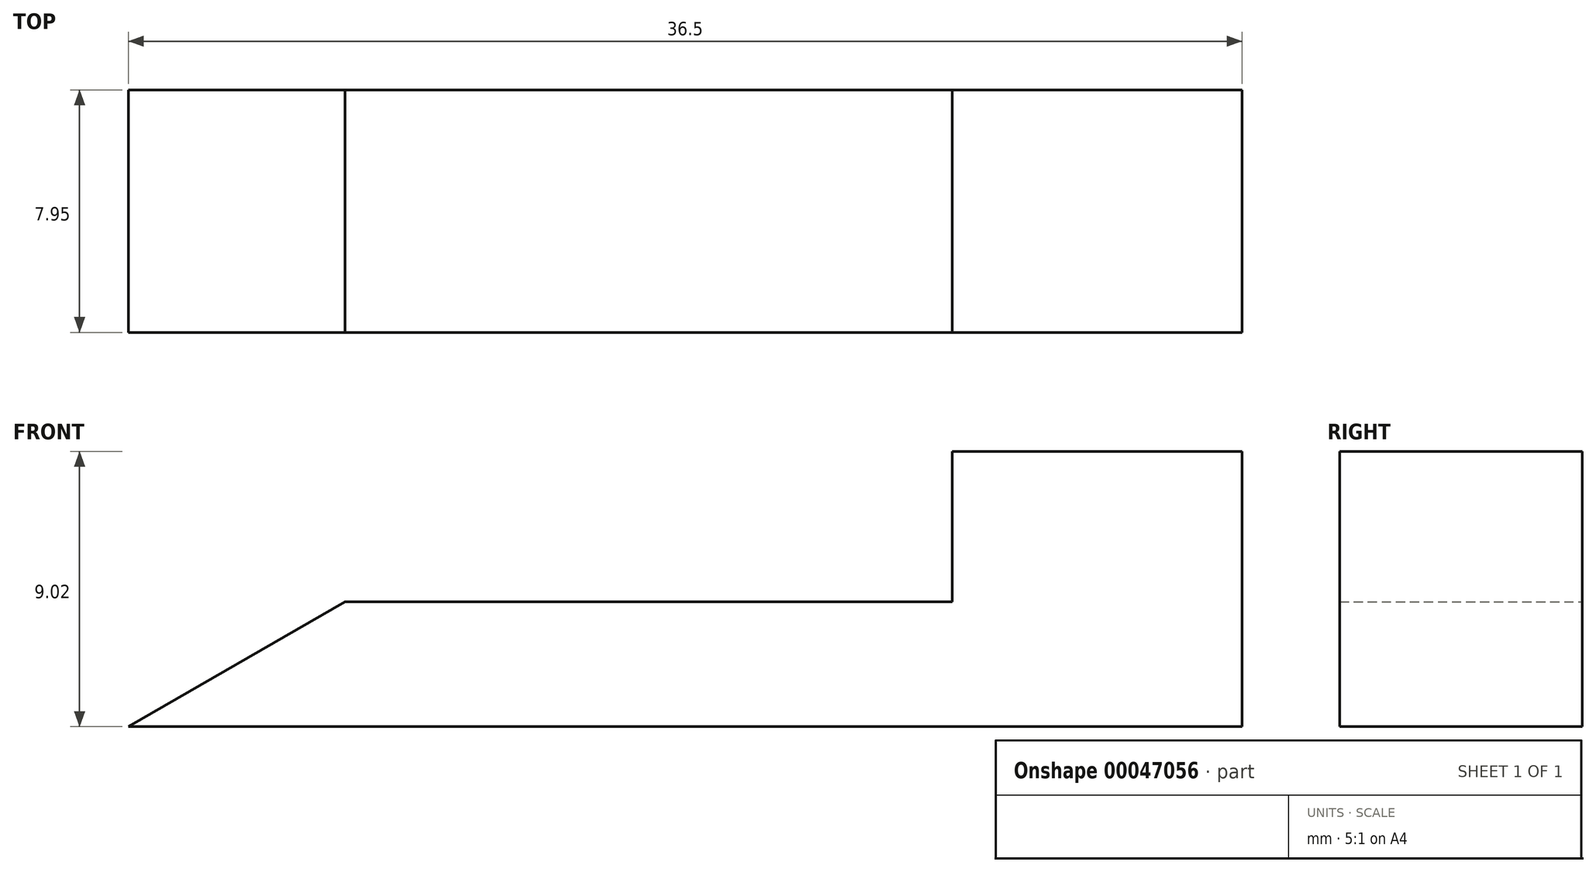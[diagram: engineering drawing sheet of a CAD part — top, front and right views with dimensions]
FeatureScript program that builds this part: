
annotation { "Feature Type Name" : "Feature", "Feature Type Description" : "" }
export const myFeature = defineFeature(function(context is Context, id is Id, definition is map)
    precondition{}
    {
        {
            var Q0;
            Q0=qCreatedBy(makeId("Front.planeOp"),FACE);
            var sketch = newSketch(context, id + "F0", { "sketchPlane" : qUnion([Q0])});
            skLineSegment(sketch, "E0", {"start": v(0, 0) * mm, "end": v(4.1, 4.1) * mm});
            skLineSegment(sketch, "E1", {"start": v(27, 9.02) * mm, "end": v(27, 9.11) * mm});
            skLineSegment(sketch, "E2", {"start": v(27, 9.02) * mm, "end": v(36.5, 9.02) * mm});
            skLineSegment(sketch, "E3", {"start": v(36.5, 9.02) * mm, "end": v(36.5, 0) * mm});
            skLineSegment(sketch, "E4", {"start": v(36.5, 0) * mm, "end": v(0, 0) * mm});
            skLineSegment(sketch, "E5", {"start": v(0, 0) * mm, "end": v(0, -0.2) * mm, "construction": true});
            skLineSegment(sketch, "E6", {"start": v(0, -0.2) * mm, "end": v(3, -0.2) * mm, "construction": true});
            skLineSegment(sketch, "E7", {"start": v(3, -0.2) * mm, "end": v(3, 0) * mm, "construction": true});
            skLineSegment(sketch, "E8", {"start": v(3, 0) * mm, "end": v(10.45, 7.45) * mm, "construction": true});
            skLineSegment(sketch, "E9", {"start": v(0, 0) * mm, "end": v(15.84, 9.14) * mm});
            skLineSegment(sketch, "E10", {"start": v(27, 4.1) * mm, "end": v(4.1, 4.1) * mm});
            skPoint(sketch, "E11", {"position": v(7.1, 4.1) * mm});
            skLineSegment(sketch, "E12", {"start": v(27, 9.11) * mm, "end": v(27, 4.1) * mm});
            skLineSegment(sketch, "E13", {"start": v(4, 2.3) * mm, "end": v(27, 2.3) * mm});
            skLineSegment(sketch, "E14", {"start": v(27, 2.3) * mm, "end": v(27, 4.1) * mm});
            skLineSegment(sketch, "E15", {"start": v(27, 0) * mm, "end": v(27, -0.2) * mm, "construction": true});
            skLineSegment(sketch, "E16", {"start": v(27, -0.2) * mm, "end": v(32, -0.2) * mm, "construction": true});
            skLineSegment(sketch, "E17", {"start": v(32, -0.2) * mm, "end": v(32, 0) * mm, "construction": true});
            skSolve(sketch);
        }
        {
            var Q0;
            {var subQ4=sQuery(id+"F0.wireOp",EDGE,"E2");Q0=makeQuery(id+"F0.imprint","IMPRINT",FACE,{"disambiguationData":[TD([[makeQuery(id+"F0.imprint","IMPRINT",EDGE,{"derivedFrom":subQ4}),-1.0]])]});}
            var Q1;
            {var subQ0=sQuery(id+"F0.wireOp",EDGE,"E13");Q1=makeQuery(id+"F0.imprint","IMPRINT",FACE,{"disambiguationData":[TD([[makeQuery(id+"F0.imprint","IMPRINT",EDGE,{"derivedFrom":subQ0}),1.0]])]});}
            extrude(context, id + "F1", {"entities" : qUnion([Q0, Q1]), "depth" : 7.95 * mm});
        }
    });
